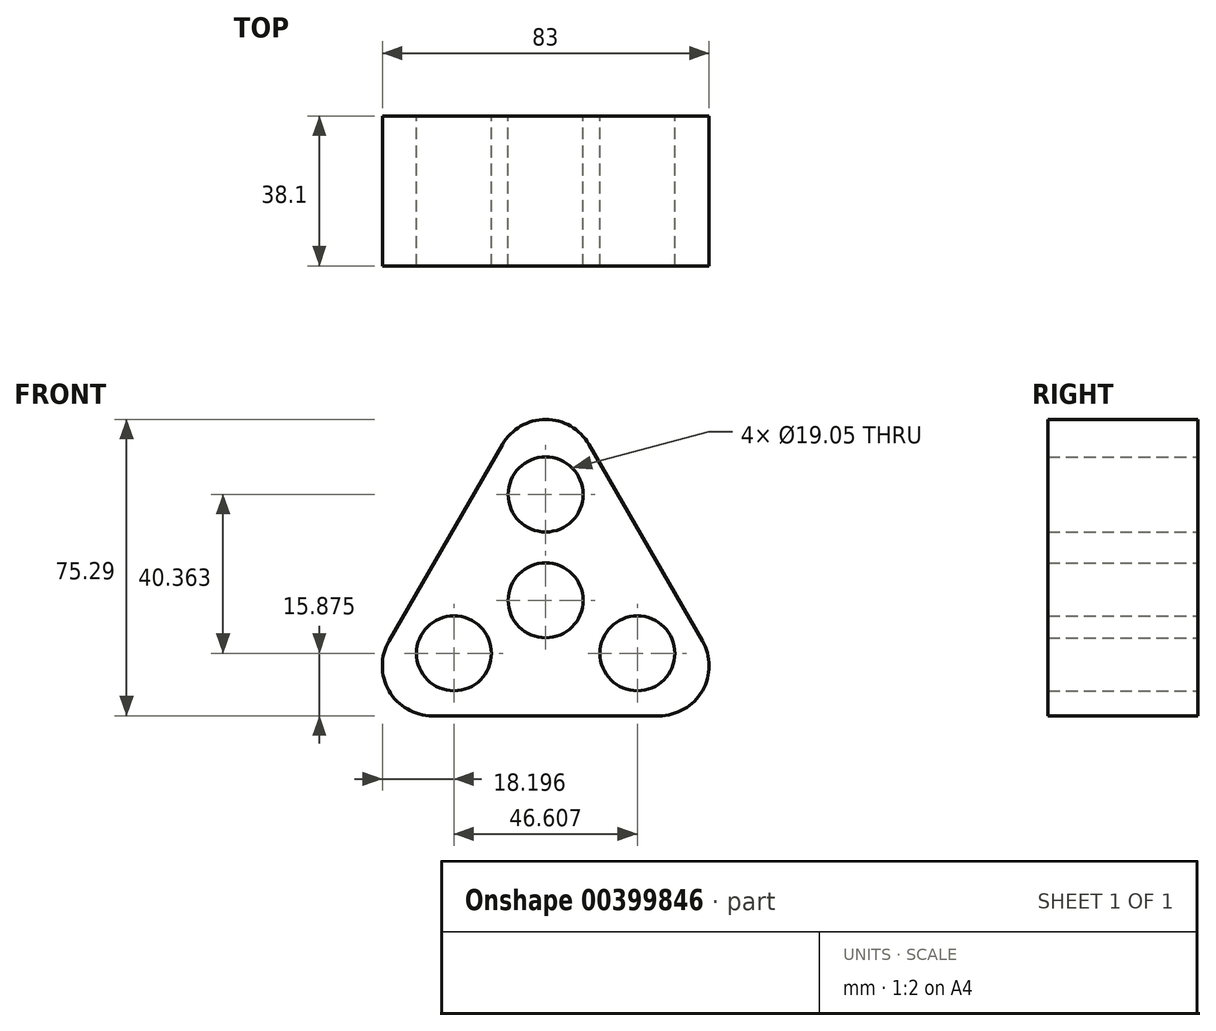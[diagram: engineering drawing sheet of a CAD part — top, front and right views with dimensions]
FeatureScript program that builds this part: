
annotation { "Feature Type Name" : "Feature", "Feature Type Description" : "" }
export const myFeature = defineFeature(function(context is Context, id is Id, definition is map)
    precondition{}
    {
        {
            var Q0;
            Q0=qCreatedBy(makeId("Front.planeOp"),FACE);
            var sketch = newSketch(context, id + "F0", { "sketchPlane" : qUnion([Q0])});
            skLineSegment(sketch, "E0", {"start": v(-22, 0) * mm, "end": v(-79.6, 0) * mm});
            skLineSegment(sketch, "E1", {"start": v(-90.6, 19.05) * mm, "end": v(-61.8, 68.94) * mm});
            skLineSegment(sketch, "E2", {"start": v(-39.8, 68.94) * mm, "end": v(-11, 19.05) * mm});
            skLineSegment(sketch, "E3.0", {"start": v(-74.1, 15.87) * mm, "end": v(-50.8, 56.24) * mm, "construction": true});
            skLineSegment(sketch, "E3.1", {"start": v(-27.5, 15.88) * mm, "end": v(-74.1, 15.87) * mm, "construction": true});
            skLineSegment(sketch, "E3.2", {"start": v(-50.8, 56.24) * mm, "end": v(-27.5, 15.88) * mm, "construction": true});
            skCircle(sketch, "E4", {"center": v(-50.8, 56.24) * mm, "radius": 9.53 * mm});
            skCircle(sketch, "E5", {"center": v(-27.5, 15.88) * mm, "radius": 9.53 * mm});
            skCircle(sketch, "E6", {"center": v(-74.1, 15.87) * mm, "radius": 9.53 * mm});
            skPoint(sketch, "E7.visualSharp", {"position": v(-50.8, 87.99) * mm});
            skArc(sketch, "E7.filletArc", {"start": v(-39.8, 68.94) * mm, "mid": v(-50.8, 75.29) * mm, "end": v(-61.8, 68.94) * mm});
            skPoint(sketch, "E8.visualSharp", {"position": v(0, 0) * mm});
            skArc(sketch, "E8.filletArc", {"start": v(-22, 0) * mm, "mid": v(-11, 6.35) * mm, "end": v(-11, 19.05) * mm});
            skPoint(sketch, "E9.visualSharp", {"position": v(-101.6, 0) * mm});
            skArc(sketch, "E9.filletArc", {"start": v(-90.6, 19.05) * mm, "mid": v(-90.6, 6.35) * mm, "end": v(-79.6, 0) * mm});
            skLineSegment(sketch, "E10", {"start": v(-50.8, 56.24) * mm, "end": v(-50.8, 15.88) * mm, "construction": true});
            skLineSegment(sketch, "E11", {"start": v(-74.1, 15.87) * mm, "end": v(-39.15, 36.06) * mm, "construction": true});
            skLineSegment(sketch, "E12", {"start": v(-27.5, 15.88) * mm, "end": v(-62.45, 36.06) * mm, "construction": true});
            skCircle(sketch, "E13", {"center": v(-50.8, 29.33) * mm, "radius": 9.53 * mm});
            skSolve(sketch);
        }
        {
            var Q0;
            Q0=makeQuery(id+"F0.imprint","IMPRINT",FACE,{"disambiguationData":[TD([[makeQuery(id+"F0.imprint","IMPRINT",EDGE,{"derivedFrom":sQuery(id+"F0.wireOp",EDGE,"E0")}),-1.0]])]});
            extrude(context, id + "F1", {"entities" : qUnion([Q0]), "depth" : 12.7 * mm});
        }
        {
            var Q0;
            Q0=makeQuery(id+"F1.opExtrude","CAP_FACE",FACE,{"disambiguationData":[OSD([sQuery(id+"F0.wireOp",EDGE,"E0"),sQuery(id+"F0.wireOp",EDGE,"E1"),sQuery(id+"F0.wireOp",EDGE,"E2"),sQuery(id+"F0.wireOp",EDGE,"E4"),sQuery(id+"F0.wireOp",EDGE,"E5"),sQuery(id+"F0.wireOp",EDGE,"E6"),sQuery(id+"F0.wireOp",EDGE,"E7.filletArc"),sQuery(id+"F0.wireOp",EDGE,"E8.filletArc"),sQuery(id+"F0.wireOp",EDGE,"E9.filletArc"),sQuery(id+"F0.wireOp",EDGE,"E13")])],"isStart":false});
            extrude(context, id + "F2", {"entities" : qUnion([Q0]), "operationType" : NewBodyOperationType.ADD, "depth" : 25.4 * mm});
        }
    });
